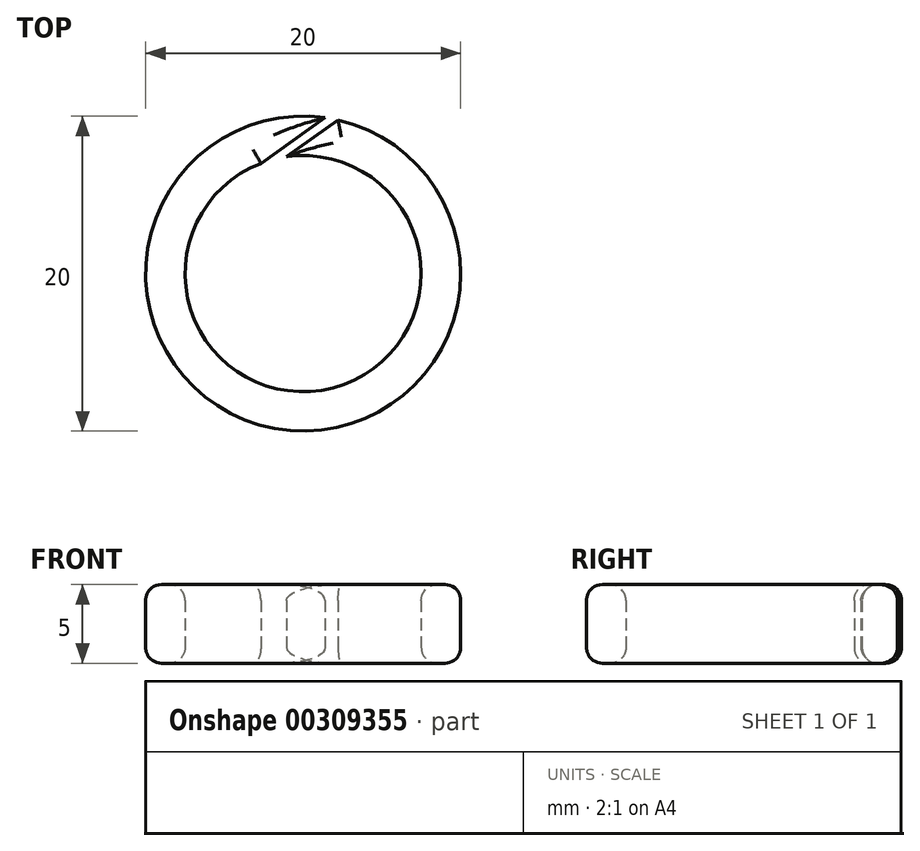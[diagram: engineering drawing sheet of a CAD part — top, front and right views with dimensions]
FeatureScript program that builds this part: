
annotation { "Feature Type Name" : "Feature", "Feature Type Description" : "" }
export const myFeature = defineFeature(function(context is Context, id is Id, definition is map)
    precondition{}
    {
        {
            var Q0;
            Q0=qCreatedBy(makeId("Top.planeOp"),FACE);
            var sketch = newSketch(context, id + "F0", { "sketchPlane" : qUnion([Q0])});
            skCircle(sketch, "E0", {"center": v(0, 0) * mm, "radius": 10 * mm});
            skCircle(sketch, "E1", {"center": v(0, 0) * mm, "radius": 7.5 * mm});
            skLineSegment(sketch, "E2", {"start": v(-2.69, 7) * mm, "end": v(1.4, 9.9) * mm});
            skLineSegment(sketch, "E3", {"start": v(-1.06, 7.43) * mm, "end": v(2.22, 9.75) * mm});
            skSolve(sketch);
        }
        {
            var Q0;
            {var subQ0=sQuery(id+"F0.wireOp",EDGE,"E2");Q0=makeQuery(id+"F0.imprint","IMPRINT",FACE,{"disambiguationData":[TD([[makeQuery(id+"F0.imprint","IMPRINT",EDGE,{"derivedFrom":subQ0}),1.0]])]});}
            extrude(context, id + "F1", {"entities" : qUnion([Q0]), "depth" : 5 * mm});
        }
        {
            var Q0;
            Q0=makeQuery(id+"F1.opExtrude","CAP_FACE",FACE,{"disambiguationData":[OSD([sQuery(id+"F0.wireOp",EDGE,"E0"),sQuery(id+"F0.wireOp",EDGE,"E1"),sQuery(id+"F0.wireOp",EDGE,"E2"),sQuery(id+"F0.wireOp",EDGE,"E3")])],"isStart":false});
            var Q1;
            Q1=makeQuery(id+"F1.opExtrude","CAP_FACE",FACE,{"disambiguationData":[OSD([sQuery(id+"F0.wireOp",EDGE,"E0"),sQuery(id+"F0.wireOp",EDGE,"E1"),sQuery(id+"F0.wireOp",EDGE,"E2"),sQuery(id+"F0.wireOp",EDGE,"E3")])],"isStart":true});
            fillet(context, id + "F2", {"entities" : qUnion([Q0, Q1]), "radius" : 1 * mm, "tangentPropagation" : true, "allowEdgeOverflow" : false});
        }
    });
